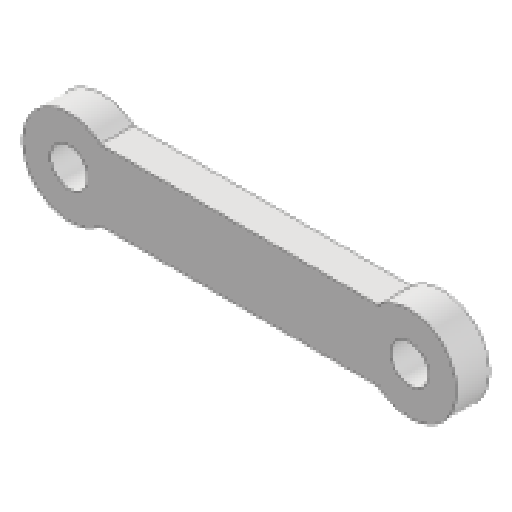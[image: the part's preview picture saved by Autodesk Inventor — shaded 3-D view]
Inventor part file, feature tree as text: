
AUTODESK INVENTOR PART (.ipt)
format: ipt  version: 2025 (Build 290162010, 162A)  size: 97,792 bytes
history: native  units: in
note: dims shown in document units (in); Inventor stores cm internally (conversion verified against a paired STEP export)
features: extrude x1, sketch x1
ambient origin geometry x8: Origin, YZ Plane, XZ Plane, XY Plane, X Axis, Y Axis, Z Axis, Center Point
bodies: Solid1 (feature_tree)
feature tree (2):
  extrude  "Extrusion1"  Depth=0.3in
  sketch  "Sketch1"  dims[d0=0.4in d1=0.3in d2=0.15in d3=0.4in d4=1.446in d5=0.16in d6=0.16in d7=0.14in d8=0.0in]
